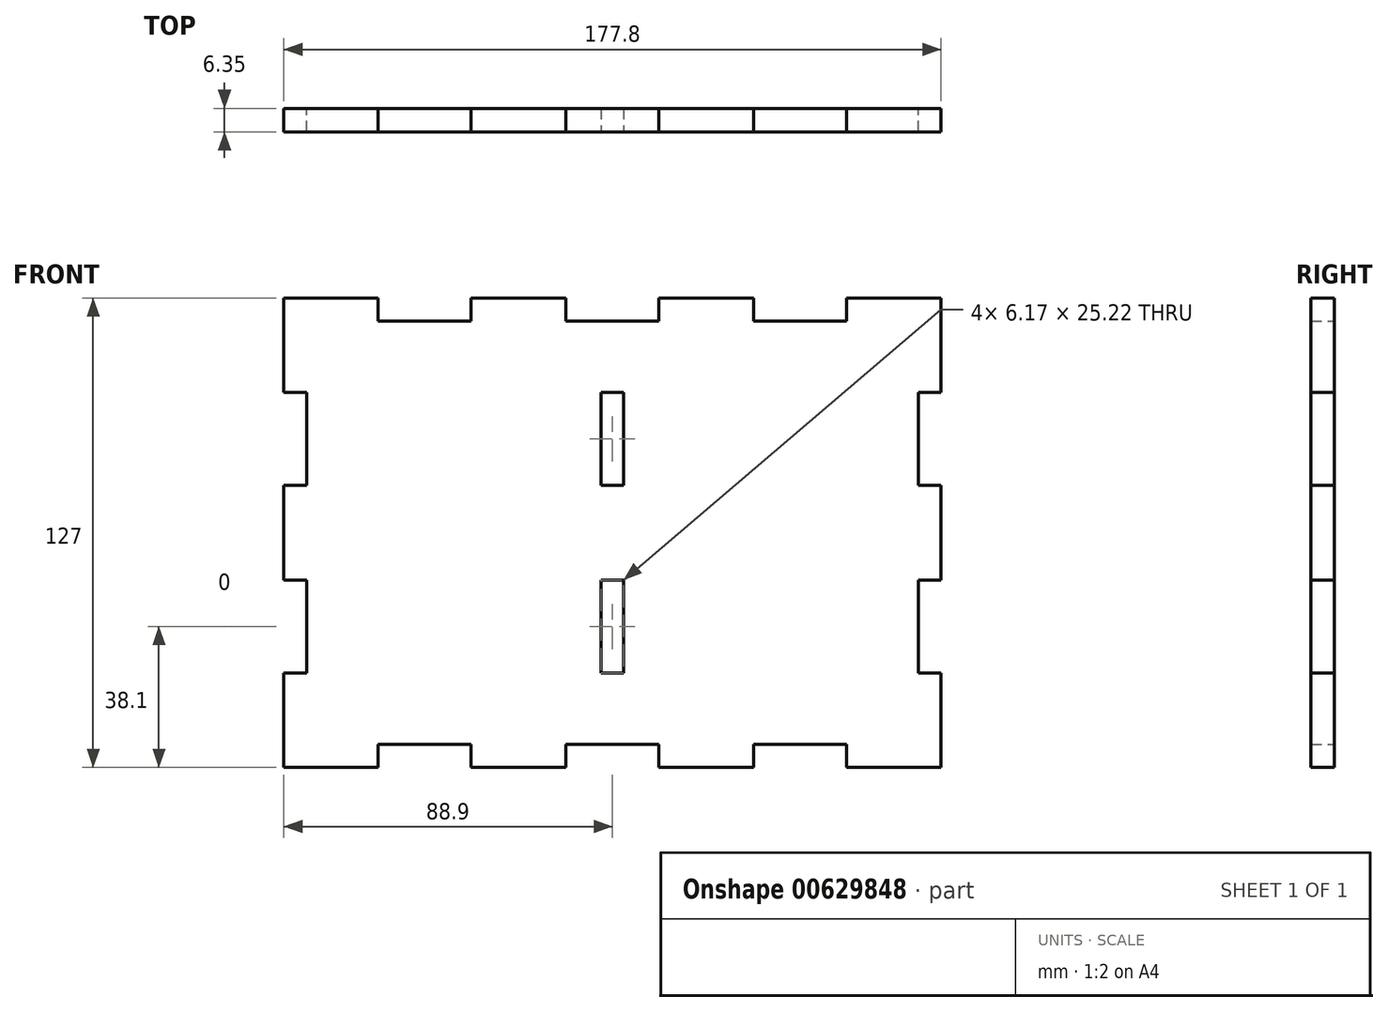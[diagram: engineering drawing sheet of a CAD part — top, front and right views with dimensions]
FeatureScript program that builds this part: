
annotation { "Feature Type Name" : "Feature", "Feature Type Description" : "" }
export const myFeature = defineFeature(function(context is Context, id is Id, definition is map)
    precondition{}
    {
        {
            var Q0;
            Q0=qCreatedBy(makeId("Front.planeOp"),FACE);
            var sketch = newSketch(context, id + "F0", { "sketchPlane" : qUnion([Q0])});
            skLineSegment(sketch, "E0.bottom", {"start": v(0, 0) * mm, "end": v(177.8, 0) * mm});
            skLineSegment(sketch, "E0.top", {"start": v(0, 127) * mm, "end": v(177.8, 127) * mm});
            skLineSegment(sketch, "E0.left", {"start": v(0, 0) * mm, "end": v(0, 127) * mm});
            skLineSegment(sketch, "E0.right", {"start": v(177.8, 0) * mm, "end": v(177.8, 127) * mm});
            skLineSegment(sketch, "E1.bottom", {"start": v(25.49, 6.17) * mm, "end": v(50.71, 6.17) * mm});
            skLineSegment(sketch, "E1.top", {"start": v(25.49, 0) * mm, "end": v(50.71, 0) * mm});
            skLineSegment(sketch, "E1.left", {"start": v(25.49, 6.17) * mm, "end": v(25.49, 0) * mm});
            skLineSegment(sketch, "E1.right", {"start": v(50.71, 6.17) * mm, "end": v(50.71, 0) * mm});
            skLineSegment(sketch, "E2.bottom", {"start": v(76.29, 6.17) * mm, "end": v(101.51, 6.17) * mm});
            skLineSegment(sketch, "E2.top", {"start": v(76.29, 0) * mm, "end": v(101.51, 0) * mm});
            skLineSegment(sketch, "E2.left", {"start": v(76.29, 6.17) * mm, "end": v(76.29, 0) * mm});
            skLineSegment(sketch, "E2.right", {"start": v(101.51, 6.17) * mm, "end": v(101.51, 0) * mm});
            skPoint(sketch, "E3", {"position": v(88.9, 6.17) * mm});
            skPoint(sketch, "E4", {"position": v(38.1, 6.17) * mm});
            skLineSegment(sketch, "E5.bottom", {"start": v(127.09, 6.17) * mm, "end": v(152.31, 6.17) * mm});
            skLineSegment(sketch, "E5.top", {"start": v(127.09, 0) * mm, "end": v(152.31, 0) * mm});
            skLineSegment(sketch, "E5.left", {"start": v(127.09, 6.17) * mm, "end": v(127.09, 0) * mm});
            skLineSegment(sketch, "E5.right", {"start": v(152.31, 6.17) * mm, "end": v(152.31, 0) * mm});
            skPoint(sketch, "E6", {"position": v(139.7, 6.17) * mm});
            skLineSegment(sketch, "E7.bottom", {"start": v(171.63, 50.71) * mm, "end": v(177.8, 50.71) * mm});
            skLineSegment(sketch, "E7.top", {"start": v(171.63, 25.49) * mm, "end": v(177.8, 25.49) * mm});
            skLineSegment(sketch, "E7.left", {"start": v(171.63, 50.71) * mm, "end": v(171.63, 25.49) * mm});
            skLineSegment(sketch, "E7.right", {"start": v(177.8, 50.71) * mm, "end": v(177.8, 25.49) * mm});
            skPoint(sketch, "E8", {"position": v(171.63, 38.1) * mm});
            skLineSegment(sketch, "E9.bottom", {"start": v(171.63, 101.51) * mm, "end": v(177.8, 101.51) * mm});
            skLineSegment(sketch, "E9.top", {"start": v(171.63, 76.29) * mm, "end": v(177.8, 76.29) * mm});
            skLineSegment(sketch, "E9.left", {"start": v(171.63, 101.51) * mm, "end": v(171.63, 76.29) * mm});
            skLineSegment(sketch, "E9.right", {"start": v(177.8, 101.51) * mm, "end": v(177.8, 76.29) * mm});
            skPoint(sketch, "E10", {"position": v(171.63, 88.9) * mm});
            skLineSegment(sketch, "E11.MirrorCS", {"start": v(0, 254) * mm, "end": v(177.8, 254) * mm});
            skLineSegment(sketch, "E12.MirrorCS", {"start": v(76.29, 247.83) * mm, "end": v(101.51, 247.83) * mm});
            skLineSegment(sketch, "E13.MirrorCS", {"start": v(76.29, 254) * mm, "end": v(101.51, 254) * mm});
            skLineSegment(sketch, "E14", {"start": v(88.9, 127) * mm, "end": v(88.9, 0) * mm, "construction": true});
            skLineSegment(sketch, "E15", {"start": v(0, 63.5) * mm, "end": v(177.8, 63.5) * mm, "construction": true});
            skLineSegment(sketch, "E16.MirrorCS", {"start": v(101.51, 120.83) * mm, "end": v(101.51, 127) * mm});
            skLineSegment(sketch, "E17.MirrorCS", {"start": v(76.29, 120.83) * mm, "end": v(76.29, 127) * mm});
            skLineSegment(sketch, "E18.MirrorCS", {"start": v(152.31, 120.83) * mm, "end": v(152.31, 127) * mm});
            skLineSegment(sketch, "E19.MirrorCS", {"start": v(127.09, 120.83) * mm, "end": v(127.09, 127) * mm});
            skLineSegment(sketch, "E20.MirrorCS", {"start": v(50.71, 120.83) * mm, "end": v(50.71, 127) * mm});
            skLineSegment(sketch, "E21.MirrorCS", {"start": v(25.49, 120.83) * mm, "end": v(25.49, 127) * mm});
            skPoint(sketch, "E22.MirrorP", {"position": v(38.1, 120.83) * mm});
            skLineSegment(sketch, "E23.MirrorCS", {"start": v(127.09, 120.83) * mm, "end": v(152.31, 120.83) * mm});
            skLineSegment(sketch, "E24.MirrorCS", {"start": v(76.29, 127) * mm, "end": v(101.51, 127) * mm});
            skLineSegment(sketch, "E25.MirrorCS", {"start": v(76.29, 120.83) * mm, "end": v(101.51, 120.83) * mm});
            skLineSegment(sketch, "E26.MirrorCS", {"start": v(25.49, 120.83) * mm, "end": v(50.71, 120.83) * mm});
            skLineSegment(sketch, "E27.MirrorCS", {"start": v(25.49, 127) * mm, "end": v(50.71, 127) * mm});
            skLineSegment(sketch, "E28.MirrorCS", {"start": v(127.09, 127) * mm, "end": v(152.31, 127) * mm});
            skPoint(sketch, "E29.MirrorP", {"position": v(88.9, 120.83) * mm});
            skPoint(sketch, "E30.MirrorP", {"position": v(139.7, 120.83) * mm});
            skLineSegment(sketch, "E31.MirrorCS", {"start": v(6.17, 25.49) * mm, "end": v(0, 25.49) * mm});
            skLineSegment(sketch, "E32.MirrorCS", {"start": v(6.17, 76.29) * mm, "end": v(0, 76.29) * mm});
            skLineSegment(sketch, "E33.MirrorCS", {"start": v(6.17, 50.71) * mm, "end": v(0, 50.71) * mm});
            skLineSegment(sketch, "E34.MirrorCS", {"start": v(6.17, 101.51) * mm, "end": v(0, 101.51) * mm});
            skLineSegment(sketch, "E35.MirrorCS", {"start": v(6.17, 50.71) * mm, "end": v(6.17, 25.49) * mm});
            skLineSegment(sketch, "E36.MirrorCS", {"start": v(6.17, 101.51) * mm, "end": v(6.17, 76.29) * mm});
            skPoint(sketch, "E37.MirrorP", {"position": v(6.17, 88.9) * mm});
            skLineSegment(sketch, "E38.MirrorCS", {"start": v(0, 101.51) * mm, "end": v(0, 76.29) * mm});
            skLineSegment(sketch, "E39.MirrorCS", {"start": v(0, 50.71) * mm, "end": v(0, 25.49) * mm});
            skPoint(sketch, "E40.MirrorP", {"position": v(6.17, 38.1) * mm});
            skSolve(sketch);
        }
        {
            var Q0;
            Q0=makeQuery(id+"F0.imprint","IMPRINT",FACE,{"disambiguationData":[TD([[makeQuery(id+"F0.imprint","IMPRINT",EDGE,{"derivedFrom":sQuery(id+"F0.wireOp",EDGE,"E1.bottom")}),1.0]])]});
            extrude(context, id + "F1", {"entities" : qUnion([Q0]), "depth" : 6.35 * mm, "offsetDistance" : 25.4 * mm});
        }
        {
            var Q0;
            Q0=makeQuery(id+"F1.opExtrude","CAP_FACE",FACE,{"disambiguationData":[OSD([sQuery(id+"F0.wireOp",EDGE,"E0.bottom"),sQuery(id+"F0.wireOp",EDGE,"E0.top"),sQuery(id+"F0.wireOp",EDGE,"E0.left"),sQuery(id+"F0.wireOp",EDGE,"E0.right"),sQuery(id+"F0.wireOp",EDGE,"E1.bottom"),sQuery(id+"F0.wireOp",EDGE,"E1.left"),sQuery(id+"F0.wireOp",EDGE,"E1.right"),sQuery(id+"F0.wireOp",EDGE,"E2.bottom"),sQuery(id+"F0.wireOp",EDGE,"E2.left"),sQuery(id+"F0.wireOp",EDGE,"E2.right"),sQuery(id+"F0.wireOp",EDGE,"E5.bottom"),sQuery(id+"F0.wireOp",EDGE,"E5.left"),sQuery(id+"F0.wireOp",EDGE,"E5.right"),sQuery(id+"F0.wireOp",EDGE,"E7.bottom"),sQuery(id+"F0.wireOp",EDGE,"E7.top"),sQuery(id+"F0.wireOp",EDGE,"E7.left"),sQuery(id+"F0.wireOp",EDGE,"E9.bottom"),sQuery(id+"F0.wireOp",EDGE,"E9.top"),sQuery(id+"F0.wireOp",EDGE,"E9.left"),sQuery(id+"F0.wireOp",EDGE,"E16.MirrorCS"),sQuery(id+"F0.wireOp",EDGE,"E17.MirrorCS"),sQuery(id+"F0.wireOp",EDGE,"E18.MirrorCS"),sQuery(id+"F0.wireOp",EDGE,"E19.MirrorCS"),sQuery(id+"F0.wireOp",EDGE,"E20.MirrorCS"),sQuery(id+"F0.wireOp",EDGE,"E21.MirrorCS"),sQuery(id+"F0.wireOp",EDGE,"E23.MirrorCS"),sQuery(id+"F0.wireOp",EDGE,"E25.MirrorCS"),sQuery(id+"F0.wireOp",EDGE,"E26.MirrorCS"),sQuery(id+"F0.wireOp",EDGE,"E31.MirrorCS"),sQuery(id+"F0.wireOp",EDGE,"E32.MirrorCS"),sQuery(id+"F0.wireOp",EDGE,"E33.MirrorCS"),sQuery(id+"F0.wireOp",EDGE,"E34.MirrorCS"),sQuery(id+"F0.wireOp",EDGE,"E35.MirrorCS"),sQuery(id+"F0.wireOp",EDGE,"E36.MirrorCS")])],"isStart":false});
            var sketch = newSketch(context, id + "F2", { "sketchPlane" : qUnion([Q0])});
            skLineSegment(sketch, "E41.bottom", {"start": v(91.99, 76.29) * mm, "end": v(85.81, 76.29) * mm});
            skLineSegment(sketch, "E41.top", {"start": v(91.99, 101.51) * mm, "end": v(85.81, 101.51) * mm});
            skLineSegment(sketch, "E41.left", {"start": v(91.99, 76.29) * mm, "end": v(91.99, 101.51) * mm});
            skLineSegment(sketch, "E41.right", {"start": v(85.81, 76.29) * mm, "end": v(85.81, 101.51) * mm});
            skPoint(sketch, "E42", {"position": v(85.81, 76.29) * mm});
            skPoint(sketch, "E43", {"position": v(85.81, 88.9) * mm});
            skLineSegment(sketch, "E44.bottom", {"start": v(85.81, 50.71) * mm, "end": v(91.99, 50.71) * mm});
            skLineSegment(sketch, "E44.top", {"start": v(85.81, 25.49) * mm, "end": v(91.99, 25.49) * mm});
            skLineSegment(sketch, "E44.left", {"start": v(91.99, 50.71) * mm, "end": v(91.99, 25.49) * mm});
            skLineSegment(sketch, "E44.right", {"start": v(85.81, 50.71) * mm, "end": v(85.81, 25.49) * mm});
            skPoint(sketch, "E45", {"position": v(91.99, 38.1) * mm});
            skPoint(sketch, "E46", {"position": v(88.9, 25.49) * mm});
            skPoint(sketch, "E47", {"position": v(88.9, 101.51) * mm});
            skSolve(sketch);
        }
        {
            var Q0;
            Q0=makeQuery(id+"F2.imprint","IMPRINT",FACE,{"disambiguationData":[TD([[makeQuery(id+"F2.imprint","IMPRINT",EDGE,{"derivedFrom":sQuery(id+"F2.wireOp",EDGE,"E41.bottom")}),-1.0]])]});
            var Q1;
            Q1=makeQuery(id+"F2.imprint","IMPRINT",FACE,{"disambiguationData":[TD([[makeQuery(id+"F2.imprint","IMPRINT",EDGE,{"derivedFrom":sQuery(id+"F2.wireOp",EDGE,"E44.bottom")}),-1.0]])]});
            extrude(context, id + "F3", {"entities" : qUnion([Q0, Q1]), "operationType" : NewBodyOperationType.REMOVE, "endBound" : BoundingType.THROUGH_ALL, "oppositeDirection" : true, "depth" : 25.4 * mm, "offsetDistance" : 25.4 * mm});
        }
    });
